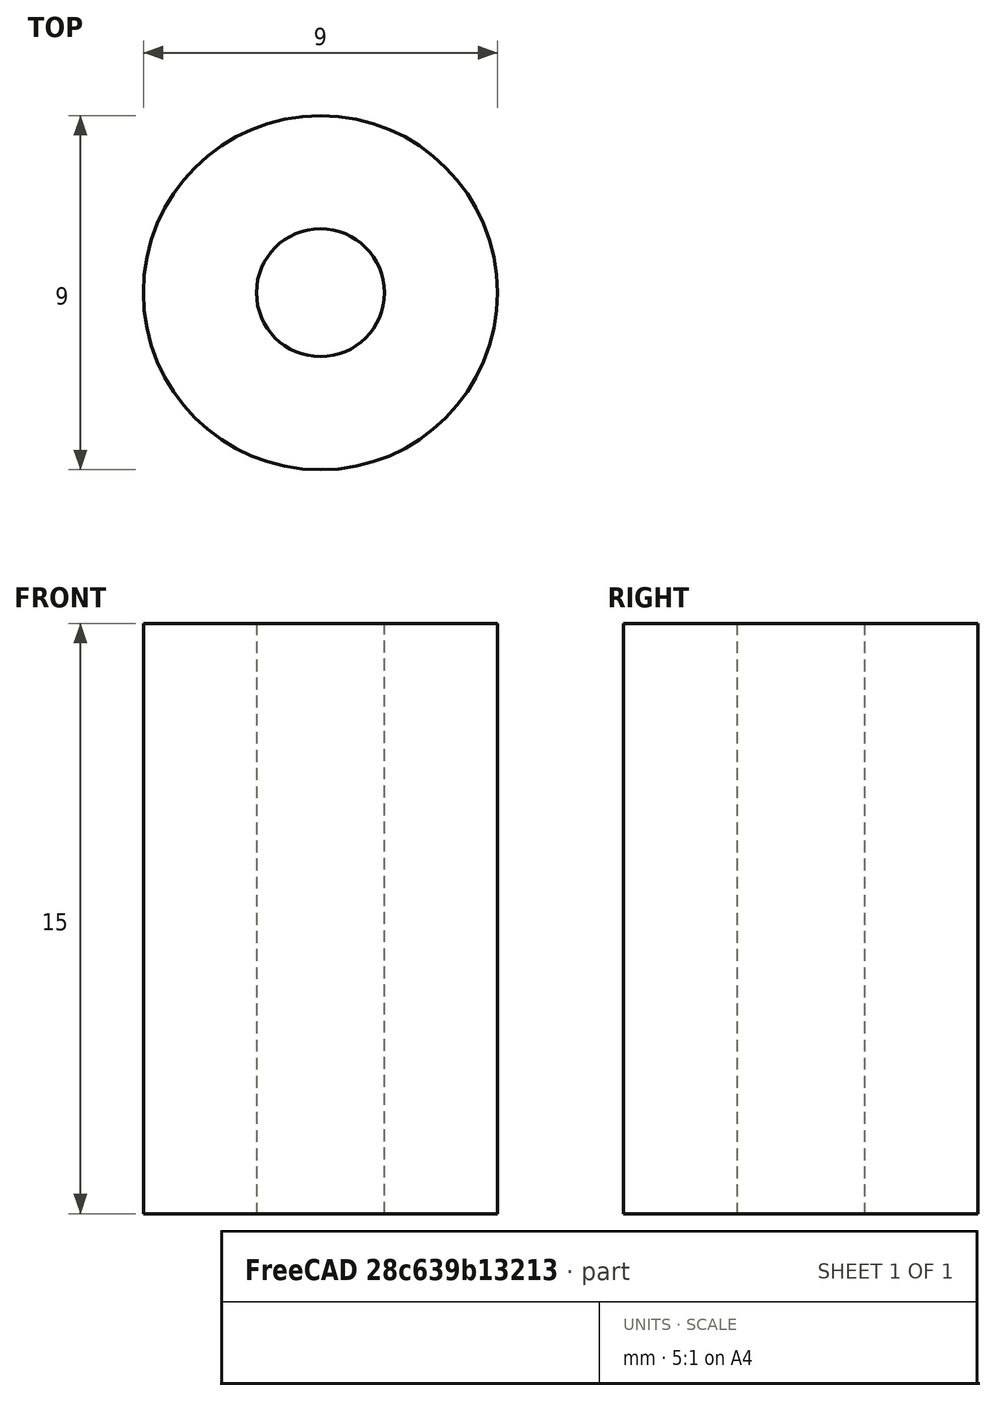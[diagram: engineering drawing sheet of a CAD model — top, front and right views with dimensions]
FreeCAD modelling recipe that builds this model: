
FCSTD DOCUMENT  (FreeCAD 0.20R29177 (Git))
Label: hélice2
License: All rights reserved
LicenseURL: http://en.wikipedia.org/wiki/All_rights_reserved
objects: Mesh::Feature×1, Sketcher::SketchObject×1, PartDesign::Pad×1, PartDesign::Body×1
note: 4 computed .brp shape members not serialized (recipe doc carries the construction recipe); baked Part::Feature solids carry a one-line shape summary decoded from their .brp

FEATURE [Mesh::Feature] Helice
FEATURE [Sketcher::SketchObject] Sketch
  FullyConstrained = true
  MapMode = 5
  Support = -> [XY_Plane]
  sketch-geometry (2):
    g0: Circle CenterX=7.4 CenterY=-6.9 CenterZ=0 NormalX=0 NormalY=0 NormalZ=1 AngleXU=0 Radius=1.625
    g1: Circle CenterX=7.4 CenterY=-6.9 CenterZ=0 NormalX=0 NormalY=0 NormalZ=1 AngleXU=0 Radius=4.5
  constraints (5):
    c: DistanceX(g-1,g0) = 7.4
    c: DistanceY(g0,g-1) = 6.9
    c: Diameter(g0) = 3.25
    c: Coincident(g1,g0)
    c: Diameter(g1) = 9
FEATURE [PartDesign::Pad] Pad
  Direction = (0,0,1)
  Length = 15
  Length2 = 10
  Profile = -> Sketch
  ReferenceAxis = -> Sketch [N_Axis]
  Type = 0
FEATURE [PartDesign::Body] Body
  Group = -> [Sketch,Pad]
  Origin = -> Origin
  Tip = -> Pad
